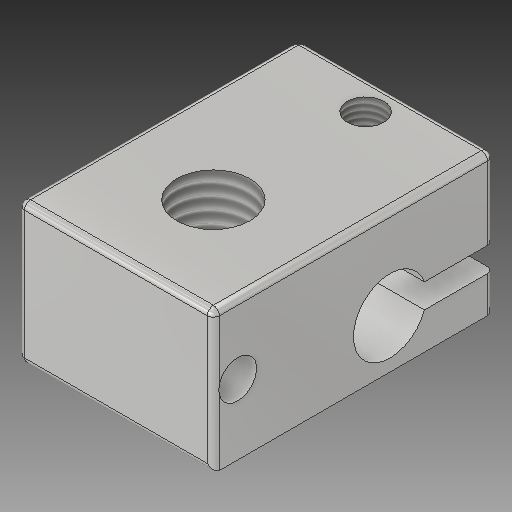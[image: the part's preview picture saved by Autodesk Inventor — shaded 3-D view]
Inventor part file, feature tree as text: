
AUTODESK INVENTOR PART (.ipt)
format: ipt  version: 2019 (Build 230136000, 136)  size: 196,608 bytes
history: native  units: mm
features: sketch x4, other x3
ambient origin geometry x8: Origin, YZ Plane, XZ Plane, XY Plane, X Axis, Y Axis, Z Axis, Center Point
bodies: Solid1 (feature_tree)
feature tree (7):
  other  "E3Dv6_Heater_Block.ipt"
  other  "Solid1::E3Dv6_Heater_Block.ipt"
  other  "TaggingFeature1"
  sketch  "Sketch1"  dims[d0=10.0mm]
  sketch  "Sketch2"
  sketch  "Sketch3"
  sketch  "Sketch4"
